# Revit family: Lollygagger Satellite Cocktail Rectangle
name_source: partatom
category: Furniture
revit_build: Autodesk Revit 2016 (Build: 20150220_1215(x64)
units: mm (PartAtom-declared; Revit-internal decimal feet)

## family parameters
Always vertical = Yes
Cut with Voids When Loaded = No
OmniClass Number = 23.40.20.00
OmniClass Title = General Furniture and Specialties
Room Calculation Point = No
Shared = No
Work Plane-Based = No

## types (11) — shared parameters
Manufacturer = Loll
Thick = 1"
Top Height = 12 7/8"
Type Image = satellite cocktail rectangle.jpg
URL = https://lolldesigns.com

## per-type parameters (varying)
| type | Finish Material | Length | Width |
| Loll-Black | Loll-Navy Blue | 40" | 22" |
| Loll-Sunset | Loll-Sunset | 42" | 23" |
| Loll-Chocolate | Loll-Chocolate | 42" | 23" |
| Loll-Sky | Loll-Sky | 42" | 23" |
| Loll-Apple | Loll-Apple | 42" | 23" |
| Loll-Leaf | Loll-Leaf | 42" | 23" |
| Loll-Evergreen | Loll-Evergreen | 42" | 23" |
| Loll-Charcoal | Loll-Charcoal | 42" | 23" |
| Loll-Sand | Loll-Sand | 42" | 23" |
| Loll-Navy Blue | Loll-Navy Blue | 40" | 22" |
| Loll-White | Loll-White | 42" | 23" |

## geometry (parser evidence)
native form markers: Sweep x3
no freeform markers — native parametric forms only
